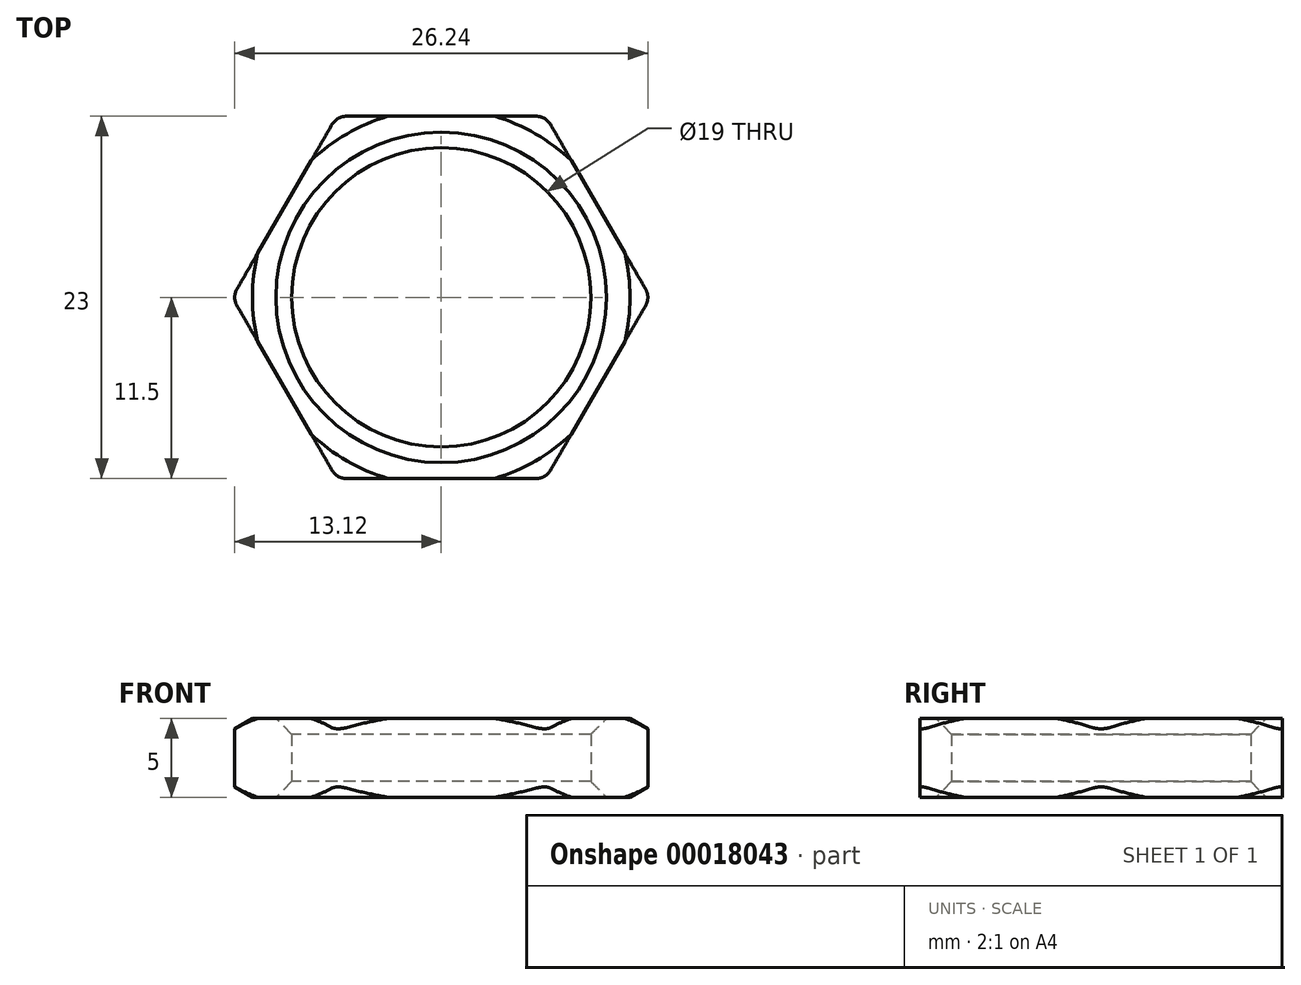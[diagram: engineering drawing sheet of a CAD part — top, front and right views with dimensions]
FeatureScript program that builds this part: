
annotation { "Feature Type Name" : "Feature", "Feature Type Description" : "" }
export const myFeature = defineFeature(function(context is Context, id is Id, definition is map)
    precondition{}
    {
        {
            var Q0;
            Q0=qCreatedBy(makeId("Top.planeOp"),FACE);
            var sketch = newSketch(context, id + "F0", { "sketchPlane" : qUnion([Q0])});
            skCircle(sketch, "E0.cCircle", {"center": v(0, 0) * mm, "radius": 11.5 * mm, "construction": true});
            skLineSegment(sketch, "E0.0", {"start": v(-6.64, 11.5) * mm, "end": v(6.64, 11.5) * mm});
            skLineSegment(sketch, "E0.1", {"start": v(6.64, 11.5) * mm, "end": v(13.28, 0) * mm});
            skLineSegment(sketch, "E0.2", {"start": v(13.28, 0) * mm, "end": v(6.64, -11.5) * mm});
            skLineSegment(sketch, "E0.3", {"start": v(6.64, -11.5) * mm, "end": v(-6.64, -11.5) * mm});
            skLineSegment(sketch, "E0.4", {"start": v(-6.64, -11.5) * mm, "end": v(-13.28, 0) * mm});
            skLineSegment(sketch, "E0.5", {"start": v(-13.28, 0) * mm, "end": v(-6.64, 11.5) * mm});
            skPoint(sketch, "E0.0.midPoint", {"position": v(0, 11.5) * mm});
            skCircle(sketch, "E1", {"center": v(0, 0) * mm, "radius": 9.5 * mm});
            skSolve(sketch);
        }
        {
            var Q0;
            Q0 = qSketchRegion(id + "F0", true);
            extrude(context, id + "F1", {"entities" : qUnion([Q0]), "depth" : 5 * mm});
        }
        {
            var Q0;
            Q0=makeQuery(id+"F1.opExtrude","SWEPT_EDGE",EDGE,{"disambiguationData":[OSD([sQuery(id+"F0.wireOp",EDGE,"E0.0"),sQuery(id+"F0.wireOp",EDGE,"E0.5")])]});
            var Q1;
            Q1=makeQuery(id+"F1.opExtrude","SWEPT_EDGE",EDGE,{"disambiguationData":[OSD([sQuery(id+"F0.wireOp",EDGE,"E0.0"),sQuery(id+"F0.wireOp",EDGE,"E0.1")])]});
            var Q2;
            Q2=makeQuery(id+"F1.opExtrude","SWEPT_EDGE",EDGE,{"disambiguationData":[OSD([sQuery(id+"F0.wireOp",EDGE,"E0.1"),sQuery(id+"F0.wireOp",EDGE,"E0.2")])]});
            var Q3;
            Q3=makeQuery(id+"F1.opExtrude","SWEPT_EDGE",EDGE,{"disambiguationData":[OSD([sQuery(id+"F0.wireOp",EDGE,"E0.2"),sQuery(id+"F0.wireOp",EDGE,"E0.3")])]});
            var Q4;
            Q4=makeQuery(id+"F1.opExtrude","SWEPT_EDGE",EDGE,{"disambiguationData":[OSD([sQuery(id+"F0.wireOp",EDGE,"E0.3"),sQuery(id+"F0.wireOp",EDGE,"E0.4")])]});
            var Q5;
            Q5=makeQuery(id+"F1.opExtrude","SWEPT_EDGE",EDGE,{"disambiguationData":[OSD([sQuery(id+"F0.wireOp",EDGE,"E0.4"),sQuery(id+"F0.wireOp",EDGE,"E0.5")])]});
            fillet(context, id + "F2", {"entities" : qUnion([Q0, Q1, Q2, Q3, Q4, Q5]), "radius" : 1 * mm, "tangentPropagation" : true, "allowEdgeOverflow" : false});
        }
        {
            var Q0;
            Q0=makeQuery(id+"F1.opExtrude","CAP_EDGE",EDGE,{"disambiguationData":[OSD([sQuery(id+"F0.wireOp",EDGE,"E1")])],"isStart":false});
            var Q1;
            Q1=makeQuery(id+"F1.opExtrude","CAP_EDGE",EDGE,{"disambiguationData":[OSD([sQuery(id+"F0.wireOp",EDGE,"E1")])],"isStart":true});
            chamfer(context, id + "F3", {"entities" : qUnion([Q0, Q1]), "width" : 1 * mm, "tangentPropagation" : true});
        }
        {
            var Q0;
            Q0=qCreatedBy(makeId("Front.planeOp"),FACE);
            var sketch = newSketch(context, id + "F4", { "sketchPlane" : qUnion([Q0])});
            skLineSegment(sketch, "E2", {"start": v(13.27, 4.26) * mm, "end": v(13.27, 5) * mm});
            skLineSegment(sketch, "E3", {"start": v(13.27, 5) * mm, "end": v(12, 5) * mm});
            skLineSegment(sketch, "E4", {"start": v(13.27, 4.26) * mm, "end": v(12, 5) * mm});
            skLineSegment(sketch, "E5", {"start": v(-13.2, 2.5) * mm, "end": v(13.45, 2.5) * mm});
            skPoint(sketch, "E6", {"position": v(-6.06, 2.5) * mm});
            skPoint(sketch, "E7", {"position": v(6.06, 2.5) * mm});
            skLineSegment(sketch, "E8.MirrorCS", {"start": v(13.27, 0.74) * mm, "end": v(13.27, 0) * mm});
            skLineSegment(sketch, "E9.MirrorCS", {"start": v(13.27, 0) * mm, "end": v(12, 0) * mm});
            skLineSegment(sketch, "E10.MirrorCS", {"start": v(13.27, 0.74) * mm, "end": v(12, 0) * mm});
            skSolve(sketch);
        }
        {
            var Q0;
            Q0 = qSketchRegion(id + "F4", true);
            var Q1;
            Q1=makeQuery(id+"F1.opExtrude","SWEPT_FACE",FACE,{"disambiguationData":[OSD([sQuery(id+"F0.wireOp",EDGE,"E1")])]});
            revolve(context, id + "F5", {"operationType" : NewBodyOperationType.REMOVE, "entities" : qUnion([Q0]), "axis" : qUnion([Q1]), "revolveType" : RevolveType.FULL, "oppositeDirection" : true});
        }
    });
